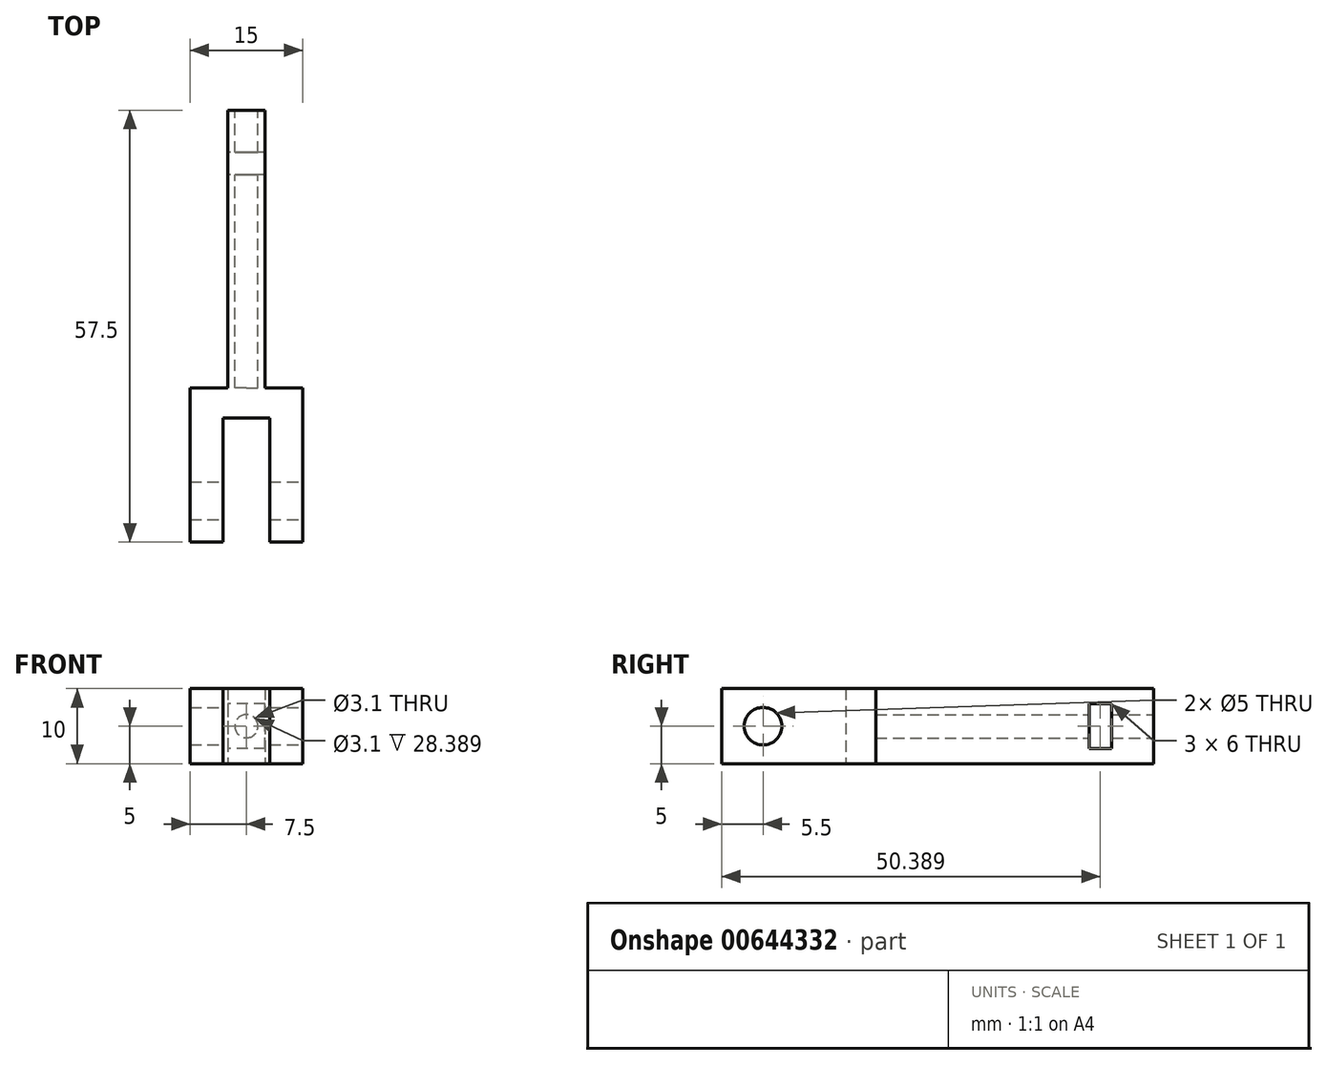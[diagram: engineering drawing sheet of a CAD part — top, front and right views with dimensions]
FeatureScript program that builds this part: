
annotation { "Feature Type Name" : "Feature", "Feature Type Description" : "" }
export const myFeature = defineFeature(function(context is Context, id is Id, definition is map)
    precondition{}
    {
        {
            var Q0;
            Q0=qCreatedBy(makeId("Front.planeOp"),FACE);
            var sketch = newSketch(context, id + "F0", { "sketchPlane" : qUnion([Q0])});
            skLineSegment(sketch, "E0.bottom", {"start": v(-2.62, 12.6) * mm, "end": v(2.7, 12.6) * mm, "construction": true});
            skLineSegment(sketch, "E0.top", {"start": v(-2.62, -12.4) * mm, "end": v(2.7, -12.4) * mm, "construction": true});
            skLineSegment(sketch, "E0.left", {"start": v(-2.62, 12.6) * mm, "end": v(-2.62, -12.4) * mm, "construction": true});
            skLineSegment(sketch, "E0.right", {"start": v(2.7, 12.6) * mm, "end": v(2.7, -12.4) * mm, "construction": true});
            skCircle(sketch, "E1", {"center": v(0, 0) * mm, "radius": 1.55 * mm});
            skLineSegment(sketch, "E2.bottom", {"start": v(2.5, 5) * mm, "end": v(-2.5, 5) * mm});
            skLineSegment(sketch, "E2.top", {"start": v(2.5, -5) * mm, "end": v(-2.5, -5) * mm});
            skLineSegment(sketch, "E2.left", {"start": v(2.5, 5) * mm, "end": v(2.5, -5) * mm});
            skLineSegment(sketch, "E2.right", {"start": v(-2.5, 5) * mm, "end": v(-2.5, -5) * mm});
            skSolve(sketch);
        }
        {
            var Q0;
            Q0=makeQuery(id+"F0.imprint","IMPRINT",FACE,{"disambiguationData":[TD([[makeQuery(id+"F0.imprint","IMPRINT",EDGE,{"derivedFrom":sQuery(id+"F0.wireOp",EDGE,"ed850d12-7903-434e-a083-8472313ea46b.bottom")}),-1.0]])]});
            var Q1;
            Q1=makeQuery(id+"F0.imprint","IMPRINT",FACE,{"disambiguationData":[TD([[makeQuery(id+"F0.imprint","IMPRINT",EDGE,{"derivedFrom":sQuery(id+"F0.wireOp",EDGE,"E1")}),-1.0]])]});
            extrude(context, id + "F1", {"entities" : qUnion([Q0, Q1]), "depth" : 37 * mm, "offsetDistance" : 25 * mm});
        }
        {
            var Q0;
            Q0=makeQuery(id+"F1.opExtrude","CAP_FACE",FACE,{"disambiguationData":[OSD([sQuery(id+"F0.wireOp",EDGE,"E1"),sQuery(id+"F0.wireOp",EDGE,"E2.bottom"),sQuery(id+"F0.wireOp",EDGE,"E2.top"),sQuery(id+"F0.wireOp",EDGE,"E2.left"),sQuery(id+"F0.wireOp",EDGE,"E2.right")])],"isStart":false});
            var sketch = newSketch(context, id + "F2", { "sketchPlane" : qUnion([Q0])});
            skLineSegment(sketch, "E3.bottom", {"start": v(7.5, 5) * mm, "end": v(-7.5, 5) * mm});
            skLineSegment(sketch, "E3.top", {"start": v(7.5, -5) * mm, "end": v(-7.5, -5) * mm});
            skLineSegment(sketch, "E3.left", {"start": v(7.5, 5) * mm, "end": v(7.5, -5) * mm});
            skLineSegment(sketch, "E3.right", {"start": v(-7.5, 5) * mm, "end": v(-7.5, -5) * mm});
            skPoint(sketch, "E3.middle", {"position": v(0, 0) * mm});
            skSolve(sketch);
        }
        {
            var Q0;
            Q0 = qSketchRegion(id + "F2", true);
            extrude(context, id + "F3", {"entities" : qUnion([Q0]), "operationType" : NewBodyOperationType.ADD, "depth" : 4 * mm, "offsetDistance" : 25 * mm});
        }
        {
            var Q0;
            Q0=makeQuery(id+"F3.opExtrude","CAP_FACE",FACE,{"disambiguationData":[OSD([sQuery(id+"F2.wireOp",EDGE,"E3.bottom"),sQuery(id+"F2.wireOp",EDGE,"E3.top"),sQuery(id+"F2.wireOp",EDGE,"E3.left"),sQuery(id+"F2.wireOp",EDGE,"E3.right")])],"isStart":false});
            var sketch = newSketch(context, id + "F4", { "sketchPlane" : qUnion([Q0])});
            skLineSegment(sketch, "E4.bottom", {"start": v(-3.1, -5) * mm, "end": v(3.1, -5) * mm, "construction": true});
            skLineSegment(sketch, "E4.top", {"start": v(-3.1, 5) * mm, "end": v(3.1, 5) * mm, "construction": true});
            skLineSegment(sketch, "E4.left", {"start": v(-3.1, -5) * mm, "end": v(-3.1, 5) * mm, "construction": true});
            skLineSegment(sketch, "E4.right", {"start": v(3.1, -5) * mm, "end": v(3.1, 5) * mm, "construction": true});
            skPoint(sketch, "E4.middle", {"position": v(0, 0) * mm});
            skLineSegment(sketch, "E5.bottom", {"start": v(-3.1, 5) * mm, "end": v(-7.5, 5) * mm});
            skLineSegment(sketch, "E5.top", {"start": v(-3.1, -5) * mm, "end": v(-7.5, -5) * mm});
            skLineSegment(sketch, "E5.left", {"start": v(-3.1, 5) * mm, "end": v(-3.1, -5) * mm});
            skLineSegment(sketch, "E5.right", {"start": v(-7.5, 5) * mm, "end": v(-7.5, -5) * mm});
            skLineSegment(sketch, "E6.bottom", {"start": v(3.1, 5) * mm, "end": v(7.5, 5) * mm});
            skLineSegment(sketch, "E6.top", {"start": v(3.1, -5) * mm, "end": v(7.5, -5) * mm});
            skLineSegment(sketch, "E6.left", {"start": v(3.1, 5) * mm, "end": v(3.1, -5) * mm});
            skLineSegment(sketch, "E6.right", {"start": v(7.5, 5) * mm, "end": v(7.5, -5) * mm});
            skSolve(sketch);
        }
        {
            var Q0;
            Q0 = qSketchRegion(id + "F4", true);
            extrude(context, id + "F5", {"entities" : qUnion([Q0]), "operationType" : NewBodyOperationType.ADD, "depth" : 16.5 * mm, "offsetDistance" : 25 * mm});
        }
        {
            var Q0;
            Q0=makeQuery(id+"F5.opExtrude","SWEPT_FACE",FACE,{"disambiguationData":[OSD([sQuery(id+"F4.wireOp",EDGE,"E5.left")])]});
            var sketch = newSketch(context, id + "F6", { "sketchPlane" : qUnion([Q0])});
            skCircle(sketch, "E7", {"center": v(-52, 0) * mm, "radius": 2.5 * mm});
            skSolve(sketch);
        }
        {
            var Q0;
            Q0 = qSketchRegion(id + "F6", true);
            extrude(context, id + "F7", {"entities" : qUnion([Q0]), "operationType" : NewBodyOperationType.REMOVE, "endBound" : BoundingType.THROUGH_ALL, "oppositeDirection" : true, "depth" : 25 * mm, "offsetDistance" : 25 * mm, "hasSecondDirection" : true, "secondDirectionBound" : SecondDirectionBoundingType.THROUGH_ALL, "secondDirectionOppositeDirection" : false, "secondDirectionDepth" : 25 * mm});
        }
        {
            var Q0;
            Q0=makeQuery(id+"F1.opExtrude","SWEPT_FACE",FACE,{"disambiguationData":[OSD([sQuery(id+"F0.wireOp",EDGE,"E2.right")])]});
            var sketch = newSketch(context, id + "F8", { "sketchPlane" : qUnion([Q0])});
            skLineSegment(sketch, "E8.bottom", {"start": v(8.61, 3) * mm, "end": v(5.61, 3) * mm});
            skLineSegment(sketch, "E8.top", {"start": v(8.61, -3) * mm, "end": v(5.61, -3) * mm});
            skLineSegment(sketch, "E8.left", {"start": v(8.61, 3) * mm, "end": v(8.61, -3) * mm});
            skLineSegment(sketch, "E8.right", {"start": v(5.61, 3) * mm, "end": v(5.61, -3) * mm});
            skPoint(sketch, "E8.middle", {"position": v(7.11, 0) * mm});
            skSolve(sketch);
        }
        {
            var Q0;
            Q0 = qSketchRegion(id + "F8", true);
            extrude(context, id + "F9", {"entities" : qUnion([Q0]), "operationType" : NewBodyOperationType.REMOVE, "endBound" : BoundingType.THROUGH_ALL, "oppositeDirection" : true, "depth" : 25 * mm, "offsetDistance" : 25 * mm});
        }
    });
